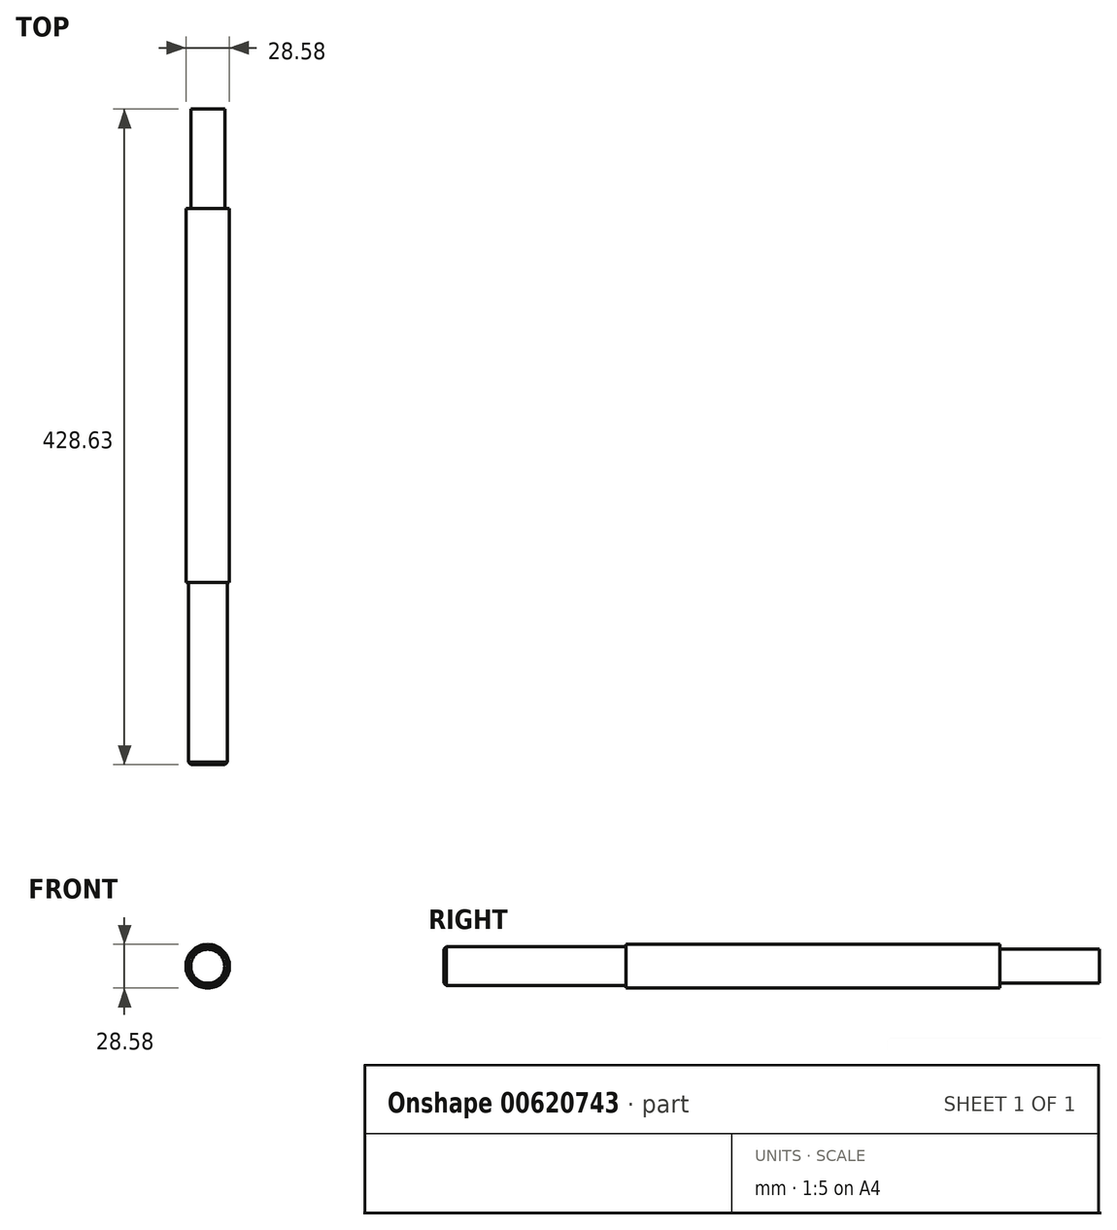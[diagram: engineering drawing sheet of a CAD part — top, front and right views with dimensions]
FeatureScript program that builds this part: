
annotation { "Feature Type Name" : "Feature", "Feature Type Description" : "" }
export const myFeature = defineFeature(function(context is Context, id is Id, definition is map)
    precondition{}
    {
        {
            var Q0;
            Q0=qCreatedBy(makeId("Front.planeOp"),FACE);
            var sketch = newSketch(context, id + "F0", { "sketchPlane" : qUnion([Q0])});
            skCircle(sketch, "E0", {"center": v(0, 0) * mm, "radius": 14.29 * mm});
            skCircle(sketch, "E1", {"center": v(0, 0) * mm, "radius": 11.11 * mm});
            skSolve(sketch);
        }
        {
            var Q0;
            Q0=makeQuery(id+"F0.imprint","IMPRINT",FACE,{"disambiguationData":[TD([[makeQuery(id+"F0.imprint","IMPRINT",EDGE,{"derivedFrom":sQuery(id+"F0.wireOp",EDGE,"E1")}),1.0]])]});
            extrude(context, id + "F1", {"entities" : qUnion([Q0]), "endBound" : BoundingType.SYMMETRIC, "depth" : 355.6 * mm, "offsetDistance" : 25.4 * mm});
        }
        {
            var Q0;
            Q0=makeQuery(id+"F0.imprint","IMPRINT",FACE,{"disambiguationData":[TD([[makeQuery(id+"F0.imprint","IMPRINT",EDGE,{"derivedFrom":sQuery(id+"F0.wireOp",EDGE,"E0")}),1.0]])]});
            extrude(context, id + "F2", {"entities" : qUnion([Q0]), "operationType" : NewBodyOperationType.ADD, "depth" : 131.78 * mm, "offsetDistance" : 25.4 * mm});
        }
        {
            var Q0;
            Q0=makeQuery(id+"F0.imprint","IMPRINT",FACE,{"disambiguationData":[TD([[makeQuery(id+"F0.imprint","IMPRINT",EDGE,{"derivedFrom":sQuery(id+"F0.wireOp",EDGE,"E0")}),1.0]])]});
            extrude(context, id + "F3", {"entities" : qUnion([Q0]), "operationType" : NewBodyOperationType.ADD, "oppositeDirection" : true, "depth" : 112.73 * mm, "offsetDistance" : 25.4 * mm});
        }
        {
            var Q0;
            Q0=qCreatedBy(makeId("Front.planeOp"),FACE);
            var sketch = newSketch(context, id + "F4", { "sketchPlane" : qUnion([Q0])});
            skCircle(sketch, "E2", {"center": v(0, 0) * mm, "radius": 6.35 * mm});
            skCircle(sketch, "E3", {"center": v(0, 0) * mm, "radius": 12.7 * mm});
            skSolve(sketch);
        }
        {
            var Q0;
            Q0=makeQuery(id+"F4.imprint","IMPRINT",FACE,{"disambiguationData":[TD([[makeQuery(id+"F4.imprint","IMPRINT",EDGE,{"derivedFrom":sQuery(id+"F4.wireOp",EDGE,"E2")}),1.0]])]});
            extrude(context, id + "F5", {"entities" : qUnion([Q0]), "oppositeDirection" : true, "depth" : (2 + (1 / 8)) * mm, "offsetDistance" : 25.4 * mm});
        }
        {
            var Q0;
            Q0=makeQuery(id+"F4.imprint","IMPRINT",FACE,{"disambiguationData":[TD([[makeQuery(id+"F4.imprint","IMPRINT",EDGE,{"derivedFrom":sQuery(id+"F4.wireOp",EDGE,"E2")}),1.0]])]});
            var Q1;
            Q1=makeQuery(id+"F4.imprint","IMPRINT",FACE,{"disambiguationData":[TD([[makeQuery(id+"F4.imprint","IMPRINT",EDGE,{"derivedFrom":sQuery(id+"F4.wireOp",EDGE,"E2")}),-1.0]])]});
            extrude(context, id + "F6", {"entities" : qUnion([Q0, Q1]), "operationType" : NewBodyOperationType.ADD, "depth" : 250.82 * mm, "offsetDistance" : 25.4 * mm});
        }
        {
            var Q0;
            Q0=makeQuery(id+"F6.opExtrude","CAP_EDGE",EDGE,{"disambiguationData":[OSD([sQuery(id+"F4.wireOp",EDGE,"E3")])],"isStart":false});
            chamfer(context, id + "F7", {"entities" : qUnion([Q0]), "chamferType" : ChamferType.OFFSET_ANGLE, "width" : 1.59 * mm, "oppositeDirection" : false, "angle" : 45 * degree, "tangentPropagation" : true});
        }
    });
